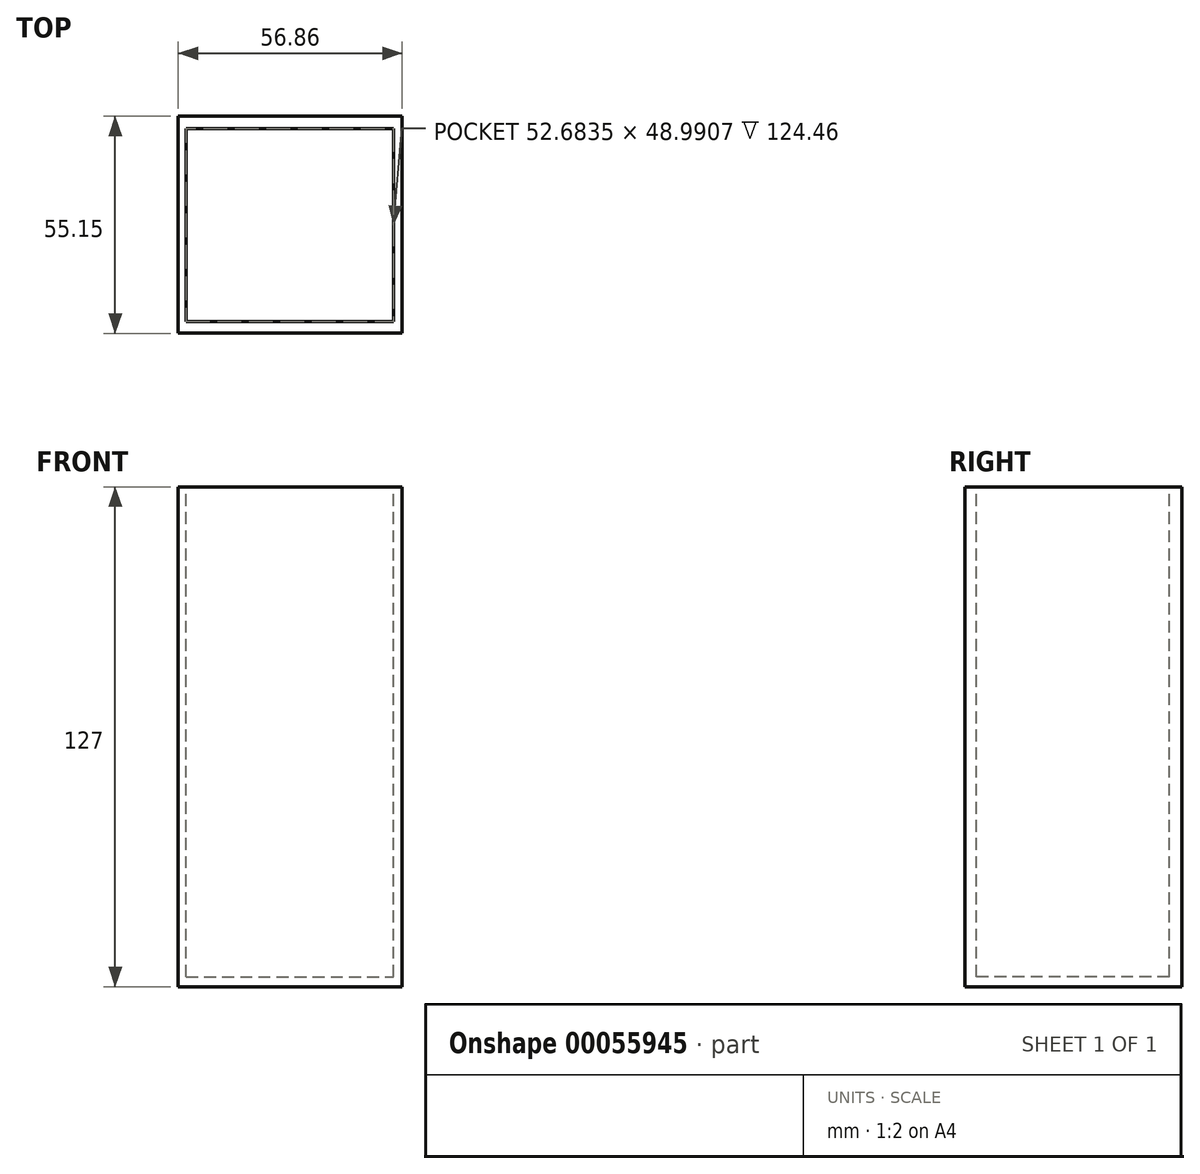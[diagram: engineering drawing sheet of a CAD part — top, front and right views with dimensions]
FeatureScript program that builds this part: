
annotation { "Feature Type Name" : "Feature", "Feature Type Description" : "" }
export const myFeature = defineFeature(function(context is Context, id is Id, definition is map)
    precondition{}
    {
        {
            var Q0;
            Q0=qCreatedBy(makeId("Top.planeOp"),FACE);
            var sketch = newSketch(context, id + "F0", { "sketchPlane" : qUnion([Q0])});
            skLineSegment(sketch, "E0.bottom", {"start": v(-23.63, 27.08) * mm, "end": v(33.23, 27.08) * mm});
            skLineSegment(sketch, "E0.top", {"start": v(-23.63, -28.07) * mm, "end": v(33.23, -28.07) * mm});
            skLineSegment(sketch, "E0.left", {"start": v(-23.63, 27.08) * mm, "end": v(-23.63, -28.07) * mm});
            skLineSegment(sketch, "E0.right", {"start": v(33.23, 27.08) * mm, "end": v(33.23, -28.07) * mm});
            skSolve(sketch);
        }
        {
            var Q0;
            Q0 = qSketchRegion(id + "F0", true);
            extrude(context, id + "F1", {"entities" : qUnion([Q0]), "depth" : 127 * mm});
        }
        {
            var Q0;
            Q0=makeQuery(id+"F1.opExtrude","CAP_FACE",FACE,{"disambiguationData":[OSD([sQuery(id+"F0.wireOp",EDGE,"E0.bottom"),sQuery(id+"F0.wireOp",EDGE,"E0.top"),sQuery(id+"F0.wireOp",EDGE,"E0.left"),sQuery(id+"F0.wireOp",EDGE,"E0.right")])],"isStart":false});
            var sketch = newSketch(context, id + "F2", { "sketchPlane" : qUnion([Q0])});
            skLineSegment(sketch, "E1.bottom", {"start": v(-21.66, 23.88) * mm, "end": v(31.02, 23.88) * mm});
            skLineSegment(sketch, "E1.top", {"start": v(-21.66, -25.11) * mm, "end": v(31.02, -25.11) * mm});
            skLineSegment(sketch, "E1.left", {"start": v(-21.66, 23.88) * mm, "end": v(-21.66, -25.11) * mm});
            skLineSegment(sketch, "E1.right", {"start": v(31.02, 23.88) * mm, "end": v(31.02, -25.11) * mm});
            skSolve(sketch);
        }
        {
            var Q0;
            Q0 = qSketchRegion(id + "F2", true);
            extrude(context, id + "F3", {"entities" : qUnion([Q0]), "operationType" : NewBodyOperationType.REMOVE, "oppositeDirection" : true, "depth" : 124.46 * mm});
        }
    });
